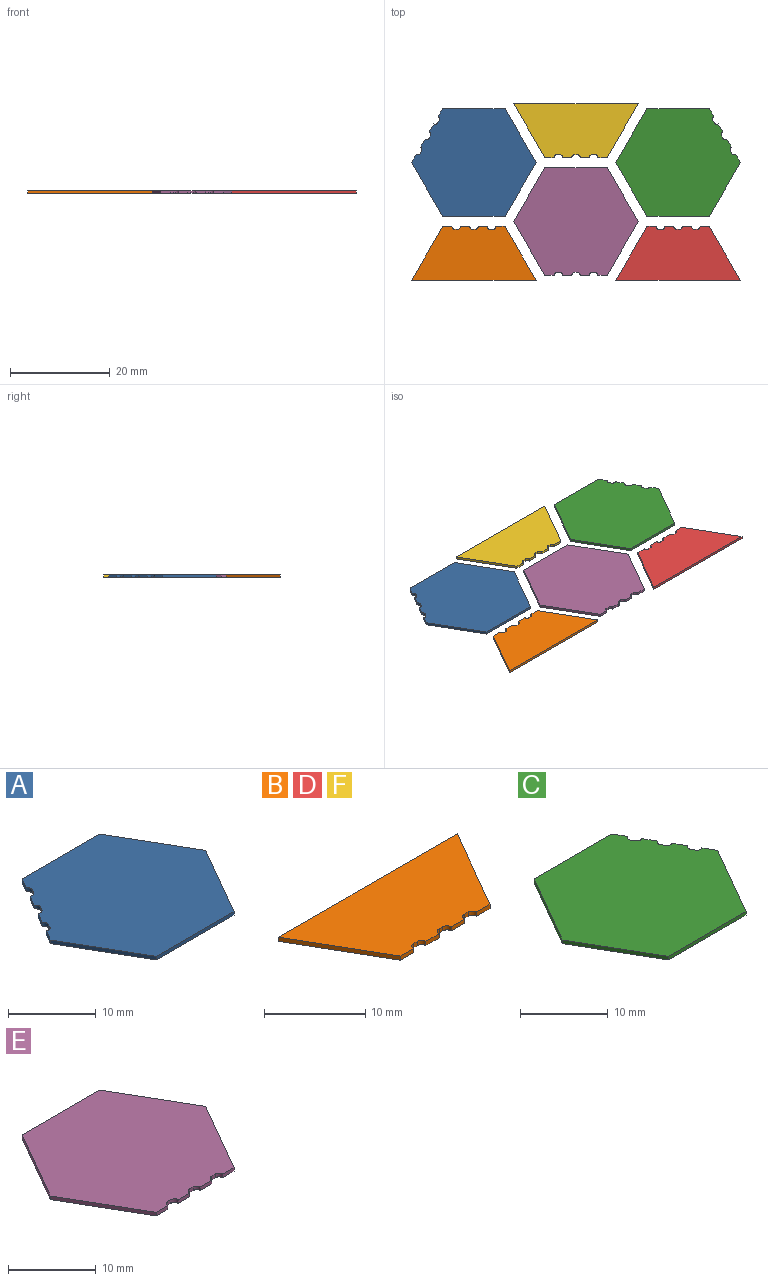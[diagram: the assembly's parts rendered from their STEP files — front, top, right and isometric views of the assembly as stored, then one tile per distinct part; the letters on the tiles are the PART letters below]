
ASSEMBLY  parts=6 mates=5
PART A: 20 faces, bbox 25x21.7x0.5 mm
  f0: plane 1.6x0.93mm, normal (-0.87,0.5,0), area 0.9mm2, adj f9,f10,f14,f19
  f1: plane 1.6x0.93mm, normal (-0.87,0.5,0), area 0.9mm2, adj f9,f10,f11,f16
  f2: plane 1.6x0.93mm, normal (-0.87,0.5,0), area 0.9mm2, adj f6,f9,f10,f13
  f3: plane 12.5x0.5mm, normal (0,-1,0), area 6.2mm2, adj f4,f8,f9,f10
  f4: plane 10.83x6.25mm, normal (0.87,-0.5,0), area 6.3mm2, adj f3,f5,f9,f10
  f5: plane 10.83x6.25mm, normal (0.87,0.5,0), area 6.3mm2, adj f4,f6,f9,f10
  f6: plane 12.5x0.5mm, normal (0,1,0), area 6.2mm2, adj f2,f5,f9,f10
  f7: plane 1.6x0.93mm, normal (-0.87,0.5,0), area 0.9mm2, adj f8,f9,f10,f17
  f8: plane 10.83x6.25mm, normal (-0.87,-0.5,0), area 6.3mm2, adj f3,f7,f9,f10
  f9: plane 25x21.65mm, normal (0,0,1), area 403.4mm2, adj f0,f1,f2,f3,f4,f5,f6,f7
  f10: plane 25x21.65mm, normal (0,0,-1), area 403.4mm2, adj f0,f1,f2,f3,f4,f5,f6,f7
  f11: cylinder r=0.6mm len=0.82mm, axis (0,0,1), area 0.5mm2, adj f1,f9,f10,f12
  f12: plane 0.5x0.43mm, normal (-0.87,0.5,0), area 0.2mm2, adj f9,f10,f11,f13
  f13: cylinder r=0.6mm len=0.82mm, axis (0,0,1), area 0.5mm2, adj f2,f9,f10,f12
  f14: cylinder r=0.6mm len=0.82mm, axis (0,0,1), area 0.5mm2, adj f0,f9,f10,f15
  f15: plane 0.5x0.43mm, normal (-0.87,0.5,0), area 0.3mm2, adj f9,f10,f14,f16
  f16: cylinder r=0.6mm len=0.82mm, axis (0,0,1), area 0.5mm2, adj f1,f9,f10,f15
  f17: cylinder r=0.6mm len=0.82mm, axis (0,0,1), area 0.5mm2, adj f7,f9,f10,f18
  f18: plane 0.5x0.43mm, normal (-0.87,0.5,0), area 0.3mm2, adj f9,f10,f17,f19
  f19: cylinder r=0.6mm len=0.82mm, axis (0,0,1), area 0.5mm2, adj f0,f9,f10,f18
PART B: 18 faces, bbox 25x10.8x0.5 mm
  f0: plane 1.85x0.5mm, normal (0,-1,0), area 0.9mm2, adj f6,f7,f11,f16
  f1: plane 1.85x0.5mm, normal (0,-1,0), area 0.9mm2, adj f6,f7,f8,f13
  f2: plane 1.85x0.5mm, normal (0,-1,0), area 0.9mm2, adj f3,f6,f7,f10
  f3: plane 10.83x6.25mm, normal (-0.87,-0.5,0), area 6.3mm2, adj f2,f6,f7,f17
  f4: plane 1.85x0.5mm, normal (0,-1,0), area 0.9mm2, adj f5,f6,f7,f14
  f5: plane 10.83x6.25mm, normal (0.87,-0.5,0), area 6.3mm2, adj f4,f6,f7,f17
  f6: plane 25x10.83mm, normal (0,0,1), area 200.4mm2, adj f0,f1,f2,f3,f4,f5,f8,f9
  f7: plane 25x10.83mm, normal (0,0,-1), area 200.4mm2, adj f0,f1,f2,f3,f4,f5,f8,f9
  f8: cylinder r=0.6mm len=0.6mm, axis (0,0,1), area 0.5mm2, adj f1,f6,f7,f9
  f9: plane 0.5x0.5mm, normal (0,-1,0), area 0.3mm2, adj f6,f7,f8,f10
  f10: cylinder r=0.6mm len=0.6mm, axis (0,0,1), area 0.5mm2, adj f2,f6,f7,f9
  f11: cylinder r=0.6mm len=0.6mm, axis (0,0,1), area 0.5mm2, adj f0,f6,f7,f12
  f12: plane 0.5x0.5mm, normal (0,-1,0), area 0.3mm2, adj f6,f7,f11,f13
  f13: cylinder r=0.6mm len=0.6mm, axis (0,0,1), area 0.5mm2, adj f1,f6,f7,f12
  f14: cylinder r=0.6mm len=0.6mm, axis (0,0,1), area 0.5mm2, adj f4,f6,f7,f15
  f15: plane 0.5x0.5mm, normal (0,-1,0), area 0.3mm2, adj f6,f7,f14,f16
  f16: cylinder r=0.6mm len=0.6mm, axis (0,0,1), area 0.5mm2, adj f0,f6,f7,f15
  f17: plane 25x0.5mm, normal (0,1,0), area 12.5mm2, adj f3,f5,f6,f7
PART C: 20 faces, bbox 25x21.7x0.5 mm
  f0: plane 1.6x0.93mm, normal (0.87,0.5,0), area 0.9mm2, adj f9,f10,f14,f19
  f1: plane 1.6x0.93mm, normal (0.87,0.5,0), area 0.9mm2, adj f9,f10,f11,f16
  f2: plane 1.6x0.93mm, normal (0.87,0.5,0), area 0.9mm2, adj f6,f9,f10,f13
  f3: plane 10.83x6.25mm, normal (-0.87,0.5,0), area 6.3mm2, adj f4,f8,f9,f10
  f4: plane 10.83x6.25mm, normal (-0.87,-0.5,0), area 6.3mm2, adj f3,f5,f9,f10
  f5: plane 12.5x0.5mm, normal (0,-1,0), area 6.2mm2, adj f4,f6,f9,f10
  f6: plane 10.83x6.25mm, normal (0.87,-0.5,0), area 6.3mm2, adj f2,f5,f9,f10
  f7: plane 1.6x0.93mm, normal (0.87,0.5,0), area 0.9mm2, adj f8,f9,f10,f17
  f8: plane 12.5x0.5mm, normal (0,1,0), area 6.2mm2, adj f3,f7,f9,f10
  f9: plane 25x21.65mm, normal (0,0,1), area 403.4mm2, adj f0,f1,f2,f3,f4,f5,f6,f7
  f10: plane 25x21.65mm, normal (0,0,-1), area 403.4mm2, adj f0,f1,f2,f3,f4,f5,f6,f7
  f11: cylinder r=0.6mm len=0.82mm, axis (0,0,1), area 0.5mm2, adj f1,f9,f10,f12
  f12: plane 0.5x0.43mm, normal (0.87,0.5,0), area 0.3mm2, adj f9,f10,f11,f13
  f13: cylinder r=0.6mm len=0.82mm, axis (0,0,1), area 0.5mm2, adj f2,f9,f10,f12
  f14: cylinder r=0.6mm len=0.82mm, axis (0,0,1), area 0.5mm2, adj f0,f9,f10,f15
  f15: plane 0.5x0.43mm, normal (0.87,0.5,0), area 0.3mm2, adj f9,f10,f14,f16
  f16: cylinder r=0.6mm len=0.82mm, axis (0,0,1), area 0.5mm2, adj f1,f9,f10,f15
  f17: cylinder r=0.6mm len=0.82mm, axis (0,0,1), area 0.5mm2, adj f7,f9,f10,f18
  f18: plane 0.5x0.43mm, normal (0.87,0.5,0), area 0.2mm2, adj f9,f10,f17,f19
  f19: cylinder r=0.6mm len=0.82mm, axis (0,0,1), area 0.5mm2, adj f0,f9,f10,f18
PART D: same geometry as B
PART E: 20 faces, bbox 25x21.7x0.5 mm
  f0: plane 1.85x0.5mm, normal (0,-1,0), area 0.9mm2, adj f9,f10,f14,f19
  f1: plane 1.85x0.5mm, normal (0,-1,0), area 0.9mm2, adj f9,f10,f11,f16
  f2: plane 1.85x0.5mm, normal (0,-1,0), area 0.9mm2, adj f6,f9,f10,f13
  f3: plane 10.83x6.25mm, normal (0.87,0.5,0), area 6.3mm2, adj f4,f8,f9,f10
  f4: plane 12.5x0.5mm, normal (0,1,0), area 6.2mm2, adj f3,f5,f9,f10
  f5: plane 10.83x6.25mm, normal (-0.87,0.5,0), area 6.3mm2, adj f4,f6,f9,f10
  f6: plane 10.83x6.25mm, normal (-0.87,-0.5,0), area 6.3mm2, adj f2,f5,f9,f10
  f7: plane 1.85x0.5mm, normal (0,-1,0), area 0.9mm2, adj f8,f9,f10,f17
  f8: plane 10.83x6.25mm, normal (0.87,-0.5,0), area 6.3mm2, adj f3,f7,f9,f10
  f9: plane 25x21.65mm, normal (0,0,1), area 403.4mm2, adj f0,f1,f2,f3,f4,f5,f6,f7
  f10: plane 25x21.65mm, normal (0,0,-1), area 403.4mm2, adj f0,f1,f2,f3,f4,f5,f6,f7
  f11: cylinder r=0.6mm len=0.6mm, axis (0,0,1), area 0.5mm2, adj f1,f9,f10,f12
  f12: plane 0.5x0.5mm, normal (0,-1,0), area 0.3mm2, adj f9,f10,f11,f13
  f13: cylinder r=0.6mm len=0.6mm, axis (0,0,1), area 0.5mm2, adj f2,f9,f10,f12
  f14: cylinder r=0.6mm len=0.6mm, axis (0,0,1), area 0.5mm2, adj f0,f9,f10,f15
  f15: plane 0.5x0.5mm, normal (0,-1,0), area 0.3mm2, adj f9,f10,f14,f16
  f16: cylinder r=0.6mm len=0.6mm, axis (0,0,1), area 0.5mm2, adj f1,f9,f10,f15
  f17: cylinder r=0.6mm len=0.6mm, axis (0,0,1), area 0.5mm2, adj f7,f9,f10,f18
  f18: plane 0.5x0.5mm, normal (0,-1,0), area 0.3mm2, adj f9,f10,f17,f19
  f19: cylinder r=0.6mm len=0.6mm, axis (0,0,1), area 0.5mm2, adj f0,f9,f10,f18
PART F: same geometry as B
PLACE A t=(-20.17,11.76,-0.28)mm
PLACE B rot(axis=(0,0,1),180deg) t=(-20.17,-11.89,-0.28)mm
PLACE C t=(20.8,11.76,-0.28)mm
PLACE D rot(axis=(0,0,1),180deg) t=(20.8,-11.89,-0.28)mm
PLACE E t=(0.32,-0.07,-0.28)mm fixed
PLACE F t=(0.32,23.58,-0.28)mm
MATE fastened F.f6 <-> E.f9  axis (0,0,1) through (-5.93,12.76,0.22)mm
MATE fastened A.f9 <-> E.f9  axis (0,0,1) through (-13.92,0.93,0.22)mm
MATE fastened D.f6 <-> C.f9  axis (0,0,1) through (14.55,-1.07,0.22)mm
MATE fastened B.f6 <-> A.f9  axis (0,0,1) through (-26.42,-1.07,0.22)mm
MATE fastened C.f9 <-> E.f9  axis (0,0,1) through (14.55,0.93,0.22)mm
